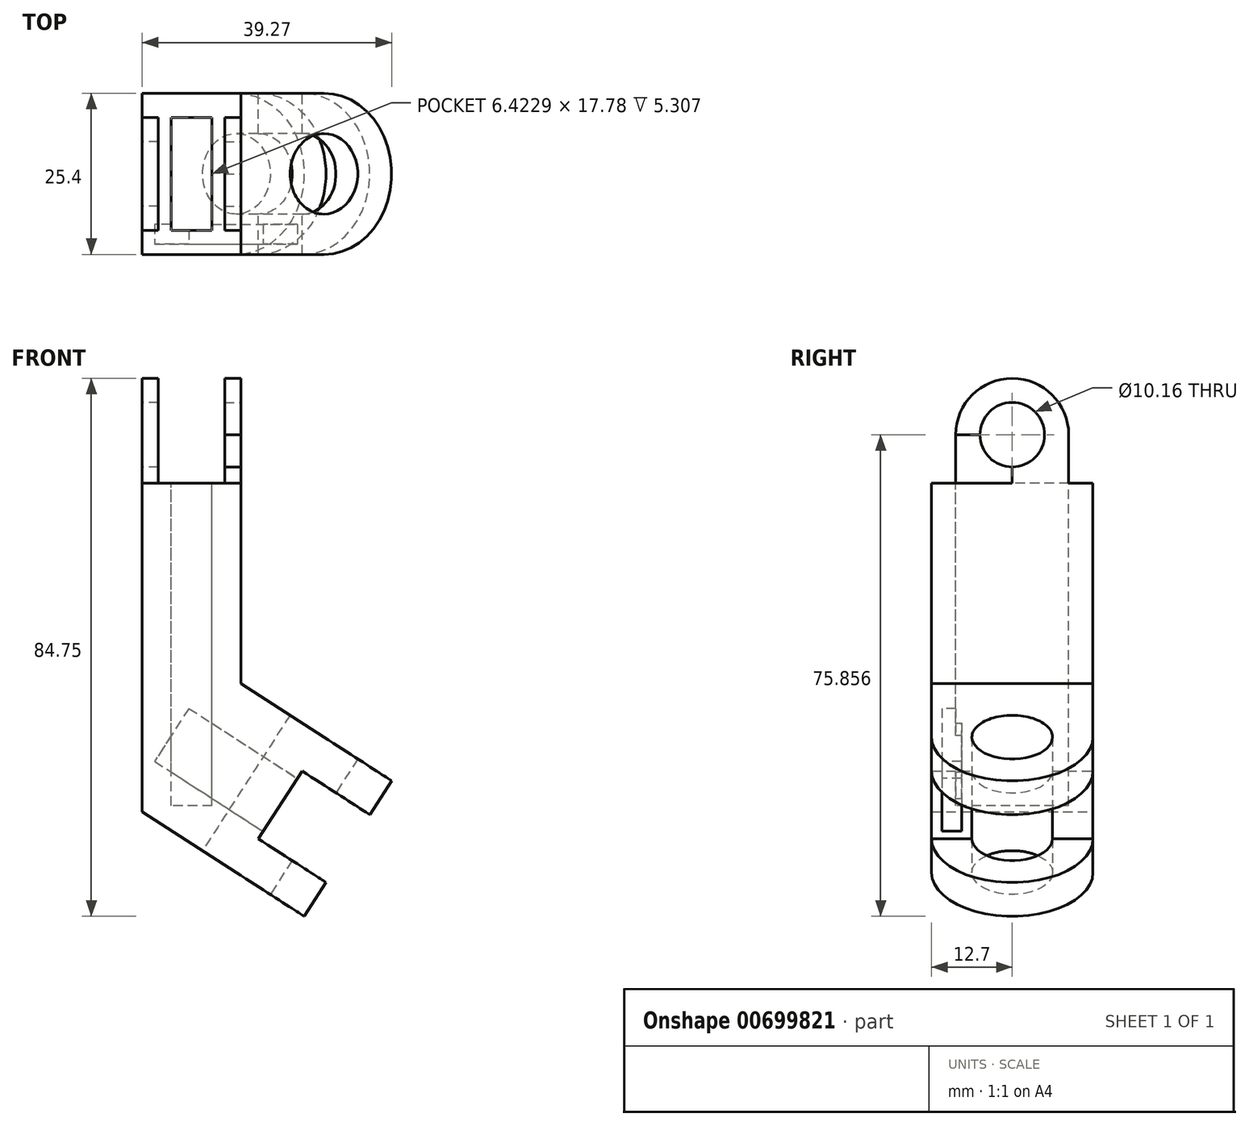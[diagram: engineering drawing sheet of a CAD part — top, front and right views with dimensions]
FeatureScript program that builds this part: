
annotation { "Feature Type Name" : "Feature", "Feature Type Description" : "" }
export const myFeature = defineFeature(function(context is Context, id is Id, definition is map)
    precondition{}
    {
        {
            var Q0;
            Q0=qCreatedBy(makeId("Front.planeOp"),FACE);
            var sketch = newSketch(context, id + "F0", { "sketchPlane" : qUnion([Q0])});
            skLineSegment(sketch, "E0", {"start": v(9.9, -37.3) * mm, "end": v(-3.19, -28.84) * mm});
            skLineSegment(sketch, "E1", {"start": v(-3.9, -58.63) * mm, "end": v(-18.71, -49.05) * mm});
            skLineSegment(sketch, "E2", {"start": v(-18.71, -49.05) * mm, "end": v(-18.71, 2.72) * mm});
            skLineSegment(sketch, "E3", {"start": v(-18.71, 2.72) * mm, "end": v(-3.19, 2.72) * mm});
            skLineSegment(sketch, "E4", {"start": v(-3.06, -57.34) * mm, "end": v(9.35, -38.14) * mm});
            skPoint(sketch, "E5.start.orphan", {"position": v(9.92, -52.43) * mm});
            skLineSegment(sketch, "E6", {"start": v(-3.06, -57.34) * mm, "end": v(-3.9, -58.63) * mm});
            skLineSegment(sketch, "E7", {"start": v(-3.9, -58.63) * mm, "end": v(9.9, -37.3) * mm});
            skPoint(sketch, "E8.orphan", {"position": v(3.03, -63.1) * mm});
            skPoint(sketch, "E9.start.orphan", {"position": v(5.9, -63.13) * mm});
            skPoint(sketch, "E10.start.orphan", {"position": v(18.01, -44.36) * mm});
            skPoint(sketch, "E11.orphan", {"position": v(16.81, -41.76) * mm});
            skLineSegment(sketch, "E12", {"start": v(-3.19, 2.72) * mm, "end": v(-3.19, -28.84) * mm});
            skPoint(sketch, "E13.orphan", {"position": v(-4.93, -27.71) * mm});
            skSolve(sketch);
        }
        {
            var Q0;
            {var subQ1=sQuery(id+"F0.wireOp",EDGE,"E0");Q0=makeQuery(id+"F0.imprint","IMPRINT",FACE,{"disambiguationData":[TD([[makeQuery(id+"F0.imprint","IMPRINT",EDGE,{"derivedFrom":subQ1}),1.0]])]});}
            extrude(context, id + "F1", {"entities" : qUnion([Q0]), "depth" : 25.4 * mm, "offsetDistance" : 25.4 * mm});
        }
        {
            var Q0;
            Q0=makeQuery(id+"F1.opExtrude","SWEPT_FACE",FACE,{"disambiguationData":[OSD([sQuery(id+"F0.wireOp",EDGE,"E12")])]});
            var sketch = newSketch(context, id + "F2", { "sketchPlane" : qUnion([Q0])});
            skLineSegment(sketch, "E14", {"start": v(-12.7, 2.72) * mm, "end": v(-12.7, 10.34) * mm});
            skCircle(sketch, "E15", {"center": v(-12.7, 10.34) * mm, "radius": 5.08 * mm});
            skLineSegment(sketch, "E16", {"start": v(-12.7, 10.34) * mm, "end": v(-3.81, 10.34) * mm});
            skArc(sketch, "E17", {"start": v(-3.81, 10.34) * mm, "mid": v(-12.7, 19.23) * mm, "end": v(-21.6, 10.34) * mm});
            skLineSegment(sketch, "E18", {"start": v(-12.7, 10.34) * mm, "end": v(-21.6, 10.34) * mm});
            skLineSegment(sketch, "E19", {"start": v(-21.6, 10.34) * mm, "end": v(-21.6, 2.72) * mm});
            skLineSegment(sketch, "E20", {"start": v(-21.6, 2.72) * mm, "end": v(-21.6, 10.34) * mm});
            skLineSegment(sketch, "E21", {"start": v(-3.81, 10.34) * mm, "end": v(-3.81, 2.72) * mm});
            skSolve(sketch);
        }
        {
            var Q0;
            {var subQ0=sQuery(id+"F2.wireOp",EDGE,"E20");Q0=makeQuery(id+"F2.imprint","IMPRINT",FACE,{"disambiguationData":[TD([[makeQuery(id+"F2.imprint","IMPRINT",EDGE,{"derivedFrom":subQ0}),-1.0]])]});}
            var Q1;
            {var subQ0=sQuery(id+"F2.wireOp",EDGE,"E21");Q1=makeQuery(id+"F2.imprint","IMPRINT",FACE,{"disambiguationData":[TD([[makeQuery(id+"F2.imprint","IMPRINT",EDGE,{"derivedFrom":subQ0}),-1.0]])]});}
            var Q2;
            {var subQ5=sQuery(id+"F2.wireOp",EDGE,"E17");Q2=makeQuery(id+"F2.imprint","IMPRINT",FACE,{"disambiguationData":[TD([[makeQuery(id+"F2.imprint","IMPRINT",EDGE,{"derivedFrom":subQ5}),1.0]])]});}
            extrude(context, id + "F3", {"entities" : qUnion([Q0, Q1, Q2]), "operationType" : NewBodyOperationType.ADD, "depth" : -2.54 * mm, "offsetDistance" : 25.4 * mm});
        }
        {
            var Q0;
            Q0=makeQuery(id+"F1.opExtrude","SWEPT_FACE",FACE,{"disambiguationData":[OSD([sQuery(id+"F0.wireOp",EDGE,"E2")])]});
            var sketch = newSketch(context, id + "F4", { "sketchPlane" : qUnion([Q0])});
            skLineSegment(sketch, "E22", {"start": v(12.7, 2.72) * mm, "end": v(12.7, 5.26) * mm});
            skCircle(sketch, "E23", {"center": v(12.7, 10.34) * mm, "radius": 5.08 * mm});
            skArc(sketch, "E24", {"start": v(21.6, 10.34) * mm, "mid": v(12.7, 19.23) * mm, "end": v(3.81, 10.34) * mm});
            skLineSegment(sketch, "E25", {"start": v(12.7, 10.34) * mm, "end": v(21.6, 10.34) * mm});
            skLineSegment(sketch, "E26", {"start": v(21.6, 10.34) * mm, "end": v(3.81, 10.34) * mm});
            skLineSegment(sketch, "E27", {"start": v(3.81, 10.34) * mm, "end": v(3.81, 2.72) * mm});
            skLineSegment(sketch, "E28", {"start": v(3.81, 2.72) * mm, "end": v(21.76, 2.72) * mm});
            skLineSegment(sketch, "E29", {"start": v(21.6, 10.34) * mm, "end": v(21.6, 2.72) * mm});
            skSolve(sketch);
        }
        {
            var Q0;
            Q0=qSketchRegion(id+"F4",true);
            extrude(context, id + "F5", {"entities" : qUnion([Q0]), "operationType" : NewBodyOperationType.ADD, "depth" : -2.54 * mm, "offsetDistance" : 25.4 * mm});
        }
        {
            var Q0;
            Q0=makeQuery(id+"F1.opExtrude","SWEPT_FACE",FACE,{"disambiguationData":[OSD([sQuery(id+"F0.wireOp",EDGE,"E1")])]});
            var sketch = newSketch(context, id + "F6", { "sketchPlane" : qUnion([Q0])});
            skArc(sketch, "E30", {"start": v(28.55, 0) * mm, "mid": v(41.25, 12.7) * mm, "end": v(28.55, 25.4) * mm});
            skCircle(sketch, "E31", {"center": v(28.55, 12.7) * mm, "radius": 5.08 * mm});
            skLineSegment(sketch, "E32", {"start": v(28.55, 25.4) * mm, "end": v(28.55, 0) * mm});
            skSolve(sketch);
        }
        {
            var Q0;
            Q0=makeQuery(id+"F1.opExtrude","SWEPT_FACE",FACE,{"disambiguationData":[OSD([sQuery(id+"F0.wireOp",EDGE,"E0")])]});
            var sketch = newSketch(context, id + "F7", { "sketchPlane" : qUnion([Q0])});
            skArc(sketch, "E33", {"start": v(28.55, -25.4) * mm, "mid": v(41.25, -12.7) * mm, "end": v(28.55, 0) * mm});
            skCircle(sketch, "E34", {"center": v(28.55, -12.7) * mm, "radius": 5.08 * mm});
            skLineSegment(sketch, "E35", {"start": v(28.55, -25.4) * mm, "end": v(28.55, 0) * mm});
            skSolve(sketch);
        }
        {
            var Q0;
            {var subQ0=sQuery(id+"F7.wireOp",EDGE,"E33");Q0=makeQuery(id+"F7.imprint","IMPRINT",FACE,{"disambiguationData":[TD([[makeQuery(id+"F7.imprint","IMPRINT",EDGE,{"derivedFrom":subQ0}),1.0]])]});}
            extrude(context, id + "F8", {"entities" : qUnion([Q0]), "operationType" : NewBodyOperationType.ADD, "depth" : -6.35 * mm, "offsetDistance" : 25.4 * mm});
        }
        {
            var Q0;
            {var subQ0=sQuery(id+"F6.wireOp",EDGE,"E30");Q0=makeQuery(id+"F6.imprint","IMPRINT",FACE,{"disambiguationData":[TD([[makeQuery(id+"F6.imprint","IMPRINT",EDGE,{"derivedFrom":subQ0}),1.0]])]});}
            extrude(context, id + "F9", {"entities" : qUnion([Q0]), "operationType" : NewBodyOperationType.ADD, "depth" : -6.35 * mm, "offsetDistance" : 25.4 * mm});
        }
        {
            var Q0;
            Q0=sQuery(id+"F6.wireOp",VERTEX,"E31.center");
            var Q1;
            Q1=makeQuery(id+"F1.opExtrude","SWEPT_BODY",BODY,{"disambiguationData":[OSD([sQuery(id+"F0.wireOp",EDGE,"E0"),sQuery(id+"F0.wireOp",EDGE,"E1"),sQuery(id+"F0.wireOp",EDGE,"E2"),sQuery(id+"F0.wireOp",EDGE,"E3"),sQuery(id+"F0.wireOp",EDGE,"E7"),sQuery(id+"F0.wireOp",EDGE,"E12")])]});
            hole(context, id + "F10", {"style" : HoleStyle.SIMPLE, "endStyle" : HoleEndStyle.BLIND, "holeDiameter" : 12.7 * mm, "majorDiameter" : 6.35 * mm, "holeDepth" : 50.8 * mm, "isTappedThrough" : true, "tappedDepth" : 12.7 * mm, "tapClearance" : 3, "locations" : qUnion([Q0]), "scope" : qUnion([Q1])});
        }
        {
            var Q0;
            {var subQ3=sQuery(id+"F0.wireOp",EDGE,"E7");Q0=makeQuery(id+"F10.hole-0.boolean.opBoolean","SPLIT",FACE,{"disambiguationData":[TD([makeQuery(id+"F1.opExtrude","CAP_FACE",FACE,{"disambiguationData":[OSD([sQuery(id+"F0.wireOp",EDGE,"E0"),sQuery(id+"F0.wireOp",EDGE,"E1"),sQuery(id+"F0.wireOp",EDGE,"E2"),sQuery(id+"F0.wireOp",EDGE,"E3"),subQ3,sQuery(id+"F0.wireOp",EDGE,"E12")])],"isStart":false})])],"derivedFrom":makeQuery(id+"F1.opExtrude","SWEPT_FACE",FACE,{"disambiguationData":[OSD([subQ3])]})});}
            var sketch = newSketch(context, id + "F11", { "sketchPlane" : qUnion([Q0])});
            skLineSegment(sketch, "E36", {"start": v(-17.78, -32.3) * mm, "end": v(-17.78, -45) * mm});
            skLineSegment(sketch, "E37", {"start": v(-19.05, -45) * mm, "end": v(-25.4, -45) * mm});
            skLineSegment(sketch, "E38.bottom", {"start": v(-20.66, -33.69) * mm, "end": v(-23.8, -33.69) * mm});
            skLineSegment(sketch, "E38.top", {"start": v(-20.66, -43.61) * mm, "end": v(-23.8, -43.61) * mm});
            skLineSegment(sketch, "E38.left", {"start": v(-20.66, -33.69) * mm, "end": v(-20.66, -43.61) * mm});
            skLineSegment(sketch, "E38.right", {"start": v(-23.8, -33.69) * mm, "end": v(-23.8, -43.61) * mm});
            skPoint(sketch, "E38.middle", {"position": v(-22.23, -38.65) * mm});
            skPoint(sketch, "E39.orphan", {"position": v(-25.4, -32.3) * mm});
            skSolve(sketch);
        }
        {
            var Q0;
            Q0=makeQuery(id+"F1.opExtrude","SWEPT_FACE",FACE,{"disambiguationData":[OSD([sQuery(id+"F0.wireOp",EDGE,"E3")])]});
            var sketch = newSketch(context, id + "F12", { "sketchPlane" : qUnion([Q0])});
            skLineSegment(sketch, "E40", {"start": v(-14.16, -7.45) * mm, "end": v(-7.74, -17.95) * mm});
            skLineSegment(sketch, "E41", {"start": v(-3.19, -25.4) * mm, "end": v(-3.19, 0) * mm});
            skLineSegment(sketch, "E42", {"start": v(-7.74, -7.45) * mm, "end": v(-14.16, -17.95) * mm});
            skLineSegment(sketch, "E43.bottom", {"start": v(-7.74, -3.81) * mm, "end": v(-14.16, -3.81) * mm});
            skLineSegment(sketch, "E43.top", {"start": v(-7.74, -21.59) * mm, "end": v(-14.16, -21.59) * mm});
            skLineSegment(sketch, "E43.left", {"start": v(-7.74, -3.81) * mm, "end": v(-7.74, -21.59) * mm});
            skLineSegment(sketch, "E43.right", {"start": v(-14.16, -3.81) * mm, "end": v(-14.16, -21.59) * mm});
            skPoint(sketch, "E43.middle", {"position": v(-10.95, -12.7) * mm});
            skPoint(sketch, "E44.orphan", {"position": v(-18.71, 0) * mm});
            skSolve(sketch);
        }
        {
            var Q0;
            {var subQ0=sQuery(id+"F12.wireOp",EDGE,"E43.top");Q0=makeQuery(id+"F12.imprint","IMPRINT",FACE,{"disambiguationData":[TD([[makeQuery(id+"F12.imprint","IMPRINT",EDGE,{"derivedFrom":subQ0}),-1.0]])]});}
            var Q1;
            {var subQ0=sQuery(id+"F12.wireOp",EDGE,"E43.right");var subQ1=sQuery(id+"F12.wireOp",EDGE,"E40");var subQ2=makeQuery(id+"F12.imprint","INTERSECT",VERTEX,{"derivedFrom":[subQ1,subQ0]});Q1=makeQuery(id+"F12.imprint","IMPRINT",FACE,{"disambiguationData":[TD([[makeQuery(id+"F12.imprint","IMPRINT",EDGE,{"disambiguationData":[TD([[subQ2,-1.0]])],"derivedFrom":subQ1}),-1.0]])]});}
            var Q2;
            {var subQ0=sQuery(id+"F12.wireOp",EDGE,"E43.left");var subQ1=sQuery(id+"F12.wireOp",EDGE,"E40");var subQ2=makeQuery(id+"F12.imprint","INTERSECT",VERTEX,{"derivedFrom":[subQ1,subQ0]});Q2=makeQuery(id+"F12.imprint","IMPRINT",FACE,{"disambiguationData":[TD([[makeQuery(id+"F12.imprint","IMPRINT",EDGE,{"disambiguationData":[TD([[subQ2,1.0]])],"derivedFrom":subQ1}),1.0]])]});}
            var Q3;
            {var subQ3=sQuery(id+"F12.wireOp",EDGE,"E43.bottom");Q3=makeQuery(id+"F12.imprint","IMPRINT",FACE,{"disambiguationData":[TD([[makeQuery(id+"F12.imprint","IMPRINT",EDGE,{"derivedFrom":subQ3}),1.0]])]});}
            extrude(context, id + "F13", {"entities" : qUnion([Q0, Q1, Q2, Q3]), "operationType" : NewBodyOperationType.REMOVE, "oppositeDirection" : true, "depth" : 50.8 * mm, "offsetDistance" : 25.4 * mm});
        }
        {
            var Q0;
            Q0=makeQuery(id+"F11.imprint","IMPRINT",FACE,{"disambiguationData":[TD([[makeQuery(id+"F11.imprint","IMPRINT",EDGE,{"derivedFrom":sQuery(id+"F11.wireOp",EDGE,"E38.bottom")}),1.0]])]});
            extrude(context, id + "F14", {"entities" : qUnion([Q0]), "operationType" : NewBodyOperationType.REMOVE, "oppositeDirection" : true, "depth" : 20.32 * mm, "offsetDistance" : 25.4 * mm});
        }
    });
